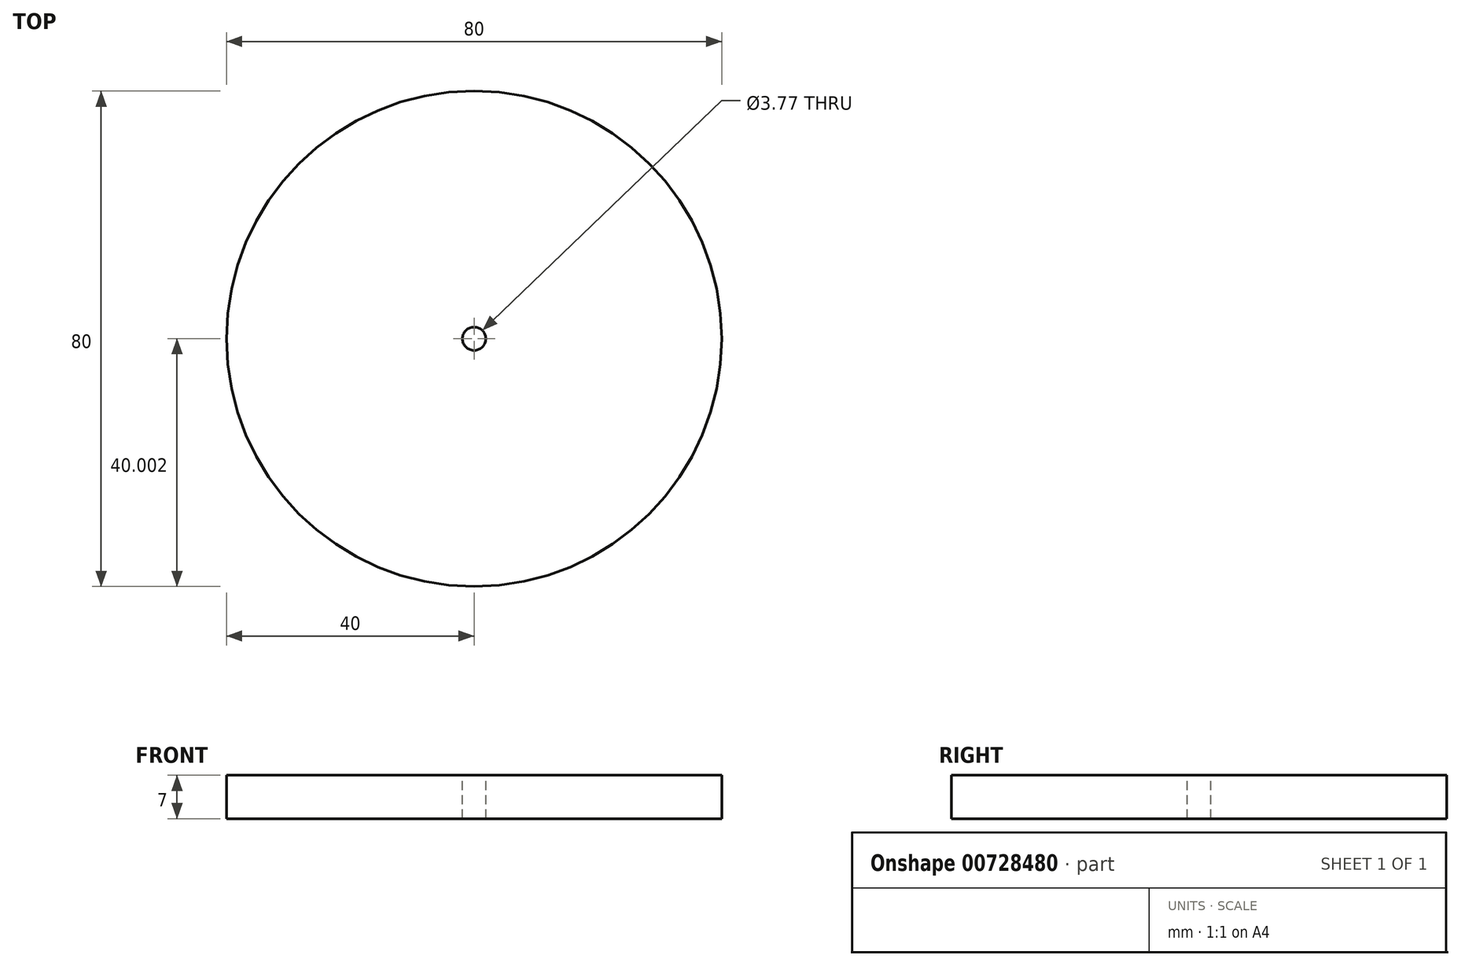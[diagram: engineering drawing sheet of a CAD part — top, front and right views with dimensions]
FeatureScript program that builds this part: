
annotation { "Feature Type Name" : "Feature", "Feature Type Description" : "" }
export const myFeature = defineFeature(function(context is Context, id is Id, definition is map)
    precondition{}
    {
        {
            var Q0;
            Q0=qCreatedBy(makeId("Top.planeOp"),FACE);
            var sketch = newSketch(context, id + "F0", { "sketchPlane" : qUnion([Q0])});
            skCircle(sketch, "E0", {"center": v(-28.4, -34.44) * mm, "radius": 40 * mm});
            skCircle(sketch, "E1", {"center": v(-28.4, -34.44) * mm, "radius": 1.89 * mm});
            skSolve(sketch);
        }
        {
            var Q0;
            Q0 = qSketchRegion(id + "F0", true);
            extrude(context, id + "F1", {"entities" : qUnion([Q0]), "oppositeDirection" : true, "depth" : 7 * mm, "offsetDistance" : 25 * mm});
        }
    });
